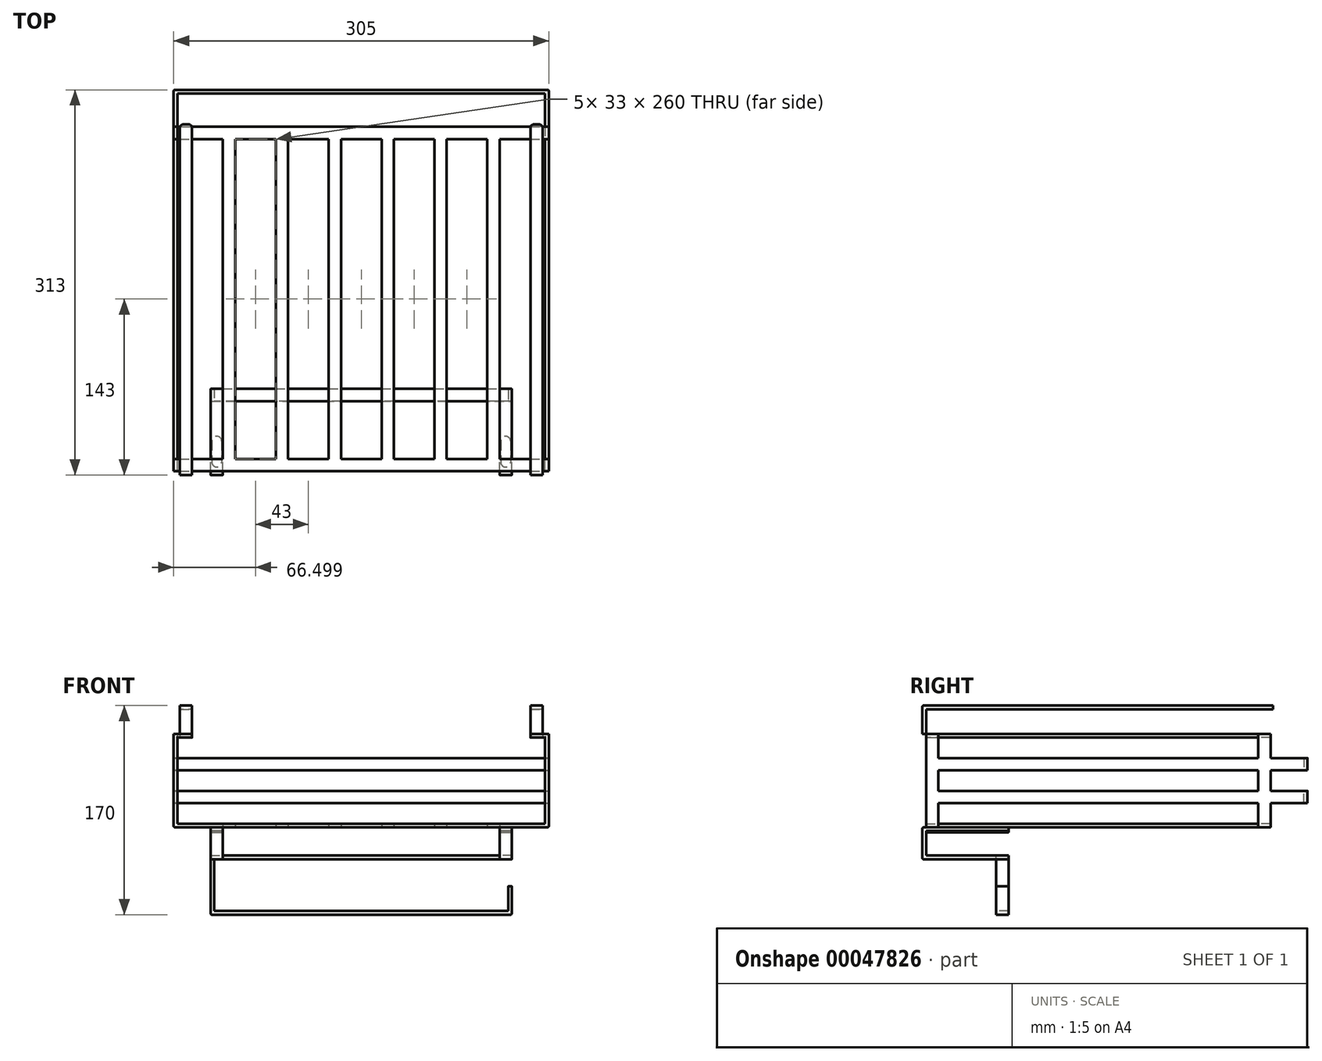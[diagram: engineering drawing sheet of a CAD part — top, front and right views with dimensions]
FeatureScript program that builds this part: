
annotation { "Feature Type Name" : "Feature", "Feature Type Description" : "" }
export const myFeature = defineFeature(function(context is Context, id is Id, definition is map)
    precondition{}
    {
        {
            var Q0;
            Q0=qCreatedBy(makeId("Top.planeOp"),FACE);
            var sketch = newSketch(context, id + "F0", { "sketchPlane" : qUnion([Q0])});
            skLineSegment(sketch, "E0.bottom", {"start": v(-169.28, 215.65) * mm, "end": v(135.72, 215.65) * mm});
            skLineSegment(sketch, "E0.top", {"start": v(-169.28, -94.35) * mm, "end": v(135.72, -94.35) * mm});
            skLineSegment(sketch, "E0.left", {"start": v(-169.28, 215.65) * mm, "end": v(-169.28, -94.35) * mm});
            skLineSegment(sketch, "E0.right", {"start": v(135.72, 215.65) * mm, "end": v(135.72, -94.35) * mm});
            skLineSegment(sketch, "E1", {"start": v(-169.28, -84.35) * mm, "end": v(135.72, -84.35) * mm});
            skLineSegment(sketch, "E2", {"start": v(-129.28, -84.35) * mm, "end": v(-129.28, 175.65) * mm});
            skLineSegment(sketch, "E3.0", {"start": v(-119.28, -84.35) * mm, "end": v(-119.28, 175.65) * mm});
            skLineSegment(sketch, "E4", {"start": v(-86.28, -84.35) * mm, "end": v(-86.28, 175.65) * mm});
            skLineSegment(sketch, "E5.0", {"start": v(-76.28, -84.35) * mm, "end": v(-76.28, 175.65) * mm});
            skLineSegment(sketch, "E6.0", {"start": v(-43.28, -84.35) * mm, "end": v(-43.28, 175.65) * mm});
            skLineSegment(sketch, "E7.0", {"start": v(-33.28, -84.35) * mm, "end": v(-33.28, 175.65) * mm});
            skLineSegment(sketch, "E8.0", {"start": v(-0.28, -84.35) * mm, "end": v(-0.28, 175.65) * mm});
            skLineSegment(sketch, "E9.0", {"start": v(9.72, -84.35) * mm, "end": v(9.72, 175.65) * mm});
            skLineSegment(sketch, "E10.0", {"start": v(42.72, -84.35) * mm, "end": v(42.72, 175.65) * mm});
            skLineSegment(sketch, "E11.0", {"start": v(52.72, -84.35) * mm, "end": v(52.72, 175.65) * mm});
            skLineSegment(sketch, "E12.0", {"start": v(85.72, -84.35) * mm, "end": v(85.72, 175.65) * mm});
            skLineSegment(sketch, "E13.0", {"start": v(95.72, -84.35) * mm, "end": v(95.72, 175.65) * mm});
            skLineSegment(sketch, "E14", {"start": v(-129.28, -42.82) * mm, "end": v(-169.28, -42.82) * mm, "construction": true});
            skLineSegment(sketch, "E15", {"start": v(95.72, -42.82) * mm, "end": v(135.72, -42.82) * mm, "construction": true});
            skLineSegment(sketch, "E16", {"start": v(-169.28, 175.65) * mm, "end": v(135.72, 175.65) * mm});
            skLineSegment(sketch, "E17.0", {"start": v(-169.28, 185.65) * mm, "end": v(135.72, 185.65) * mm});
            skPoint(sketch, "E18", {"position": v(-16.78, -94.35) * mm});
            skSolve(sketch);
        }
        {
            var Q0;
            {var subQ13=sQuery(id+"F0.wireOp",EDGE,"E17.0");Q0=makeQuery(id+"F0.imprint","IMPRINT",FACE,{"disambiguationData":[TD([[makeQuery(id+"F0.imprint","IMPRINT",EDGE,{"derivedFrom":subQ13}),-1.0]])]});}
            var Q1;
            {var subQ2=sQuery(id+"F0.wireOp",EDGE,"E2");Q1=makeQuery(id+"F0.imprint","IMPRINT",FACE,{"disambiguationData":[TD([[makeQuery(id+"F0.imprint","IMPRINT",EDGE,{"derivedFrom":subQ2}),-1.0]])]});}
            var Q2;
            {var subQ2=sQuery(id+"F0.wireOp",EDGE,"E4");Q2=makeQuery(id+"F0.imprint","IMPRINT",FACE,{"disambiguationData":[TD([[makeQuery(id+"F0.imprint","IMPRINT",EDGE,{"derivedFrom":subQ2}),-1.0]])]});}
            var Q3;
            {var subQ2=sQuery(id+"F0.wireOp",EDGE,"E6.0");Q3=makeQuery(id+"F0.imprint","IMPRINT",FACE,{"disambiguationData":[TD([[makeQuery(id+"F0.imprint","IMPRINT",EDGE,{"derivedFrom":subQ2}),-1.0]])]});}
            var Q4;
            {var subQ2=sQuery(id+"F0.wireOp",EDGE,"E8.0");Q4=makeQuery(id+"F0.imprint","IMPRINT",FACE,{"disambiguationData":[TD([[makeQuery(id+"F0.imprint","IMPRINT",EDGE,{"derivedFrom":subQ2}),-1.0]])]});}
            var Q5;
            {var subQ2=sQuery(id+"F0.wireOp",EDGE,"E10.0");Q5=makeQuery(id+"F0.imprint","IMPRINT",FACE,{"disambiguationData":[TD([[makeQuery(id+"F0.imprint","IMPRINT",EDGE,{"derivedFrom":subQ2}),-1.0]])]});}
            var Q6;
            {var subQ2=sQuery(id+"F0.wireOp",EDGE,"E12.0");Q6=makeQuery(id+"F0.imprint","IMPRINT",FACE,{"disambiguationData":[TD([[makeQuery(id+"F0.imprint","IMPRINT",EDGE,{"derivedFrom":subQ2}),-1.0]])]});}
            var Q7;
            {var subQ6=sQuery(id+"F0.wireOp",EDGE,"E0.top");Q7=makeQuery(id+"F0.imprint","IMPRINT",FACE,{"disambiguationData":[TD([[makeQuery(id+"F0.imprint","IMPRINT",EDGE,{"derivedFrom":subQ6}),1.0]])]});}
            extrude(context, id + "F1", {"entities" : qUnion([Q0, Q1, Q2, Q3, Q4, Q5, Q6, Q7]), "depth" : 3 * mm});
        }
        {
            var Q0;
            Q0=makeQuery(id+"F1.opExtrude","CAP_FACE",FACE,{"disambiguationData":[OSD([sQuery(id+"F0.wireOp",EDGE,"E0.top"),sQuery(id+"F0.wireOp",EDGE,"E0.left"),sQuery(id+"F0.wireOp",EDGE,"E0.right"),sQuery(id+"F0.wireOp",EDGE,"E1"),sQuery(id+"F0.wireOp",EDGE,"E2"),sQuery(id+"F0.wireOp",EDGE,"E3.0"),sQuery(id+"F0.wireOp",EDGE,"E4"),sQuery(id+"F0.wireOp",EDGE,"E5.0"),sQuery(id+"F0.wireOp",EDGE,"E6.0"),sQuery(id+"F0.wireOp",EDGE,"E7.0"),sQuery(id+"F0.wireOp",EDGE,"E8.0"),sQuery(id+"F0.wireOp",EDGE,"E9.0"),sQuery(id+"F0.wireOp",EDGE,"E10.0"),sQuery(id+"F0.wireOp",EDGE,"E11.0"),sQuery(id+"F0.wireOp",EDGE,"E12.0"),sQuery(id+"F0.wireOp",EDGE,"E13.0"),sQuery(id+"F0.wireOp",EDGE,"E16"),sQuery(id+"F0.wireOp",EDGE,"E17.0")])],"isStart":false});
            var sketch = newSketch(context, id + "F2", { "sketchPlane" : qUnion([Q0])});
            skLineSegment(sketch, "E19.bottom", {"start": v(-169.28, 185.65) * mm, "end": v(-166.28, 185.65) * mm});
            skLineSegment(sketch, "E19.top", {"start": v(-169.28, 175.65) * mm, "end": v(-166.28, 175.65) * mm});
            skLineSegment(sketch, "E19.left", {"start": v(-169.28, 185.65) * mm, "end": v(-169.28, 175.65) * mm});
            skLineSegment(sketch, "E19.right", {"start": v(-166.28, 185.65) * mm, "end": v(-166.28, 175.65) * mm});
            skLineSegment(sketch, "E20.bottom", {"start": v(-169.28, -94.35) * mm, "end": v(-166.28, -94.35) * mm});
            skLineSegment(sketch, "E20.top", {"start": v(-169.28, -84.35) * mm, "end": v(-166.28, -84.35) * mm});
            skLineSegment(sketch, "E20.left", {"start": v(-169.28, -94.35) * mm, "end": v(-169.28, -84.35) * mm});
            skLineSegment(sketch, "E20.right", {"start": v(-166.28, -94.35) * mm, "end": v(-166.28, -84.35) * mm});
            skLineSegment(sketch, "E21", {"start": v(-16.78, 152.07) * mm, "end": v(-16.78, 185.65) * mm, "construction": true});
            skLineSegment(sketch, "E22.MirrorCS", {"start": v(132.72, 185.65) * mm, "end": v(132.72, 175.65) * mm});
            skLineSegment(sketch, "E23.MirrorCS", {"start": v(135.72, 185.65) * mm, "end": v(135.72, 175.65) * mm});
            skLineSegment(sketch, "E24.MirrorCS", {"start": v(135.72, 185.65) * mm, "end": v(132.72, 185.65) * mm});
            skLineSegment(sketch, "E25.MirrorCS", {"start": v(135.72, 175.65) * mm, "end": v(132.72, 175.65) * mm});
            skLineSegment(sketch, "E26.MirrorCS", {"start": v(132.72, -94.35) * mm, "end": v(132.72, -84.35) * mm});
            skLineSegment(sketch, "E27.MirrorCS", {"start": v(135.72, -94.35) * mm, "end": v(135.72, -84.35) * mm});
            skLineSegment(sketch, "E28.MirrorCS", {"start": v(135.72, -84.35) * mm, "end": v(132.72, -84.35) * mm});
            skLineSegment(sketch, "E29.MirrorCS", {"start": v(135.72, -94.35) * mm, "end": v(132.72, -94.35) * mm});
            skSolve(sketch);
        }
        {
            var Q0;
            Q0=makeQuery(id+"F2.imprint","IMPRINT",FACE,{"disambiguationData":[TD([[makeQuery(id+"F2.imprint","IMPRINT",EDGE,{"derivedFrom":sQuery(id+"F2.wireOp",EDGE,"E19.bottom")}),-1.0]])]});
            var Q1;
            Q1=makeQuery(id+"F2.imprint","IMPRINT",FACE,{"disambiguationData":[TD([[makeQuery(id+"F2.imprint","IMPRINT",EDGE,{"derivedFrom":sQuery(id+"F2.wireOp",EDGE,"E22.MirrorCS")}),1.0]])]});
            var Q2;
            Q2=makeQuery(id+"F2.imprint","IMPRINT",FACE,{"disambiguationData":[TD([[makeQuery(id+"F2.imprint","IMPRINT",EDGE,{"derivedFrom":sQuery(id+"F2.wireOp",EDGE,"E26.MirrorCS")}),-1.0]])]});
            var Q3;
            Q3=makeQuery(id+"F2.imprint","IMPRINT",FACE,{"disambiguationData":[TD([[makeQuery(id+"F2.imprint","IMPRINT",EDGE,{"derivedFrom":sQuery(id+"F2.wireOp",EDGE,"E20.bottom")}),1.0]])]});
            extrude(context, id + "F3", {"entities" : qUnion([Q0, Q1, Q2, Q3]), "operationType" : NewBodyOperationType.ADD, "depth" : 70 * mm});
        }
        {
            var Q0;
            Q0=makeQuery(id+"F3.opExtrude","CAP_FACE",FACE,{"disambiguationData":[OSD([sQuery(id+"F2.wireOp",EDGE,"E19.bottom"),sQuery(id+"F2.wireOp",EDGE,"E19.top"),sQuery(id+"F2.wireOp",EDGE,"E19.left"),sQuery(id+"F2.wireOp",EDGE,"E19.right")])],"isStart":false});
            var sketch = newSketch(context, id + "F4", { "sketchPlane" : qUnion([Q0])});
            skLineSegment(sketch, "E30.bottom", {"start": v(-164.28, 185.65) * mm, "end": v(-154.28, 185.65) * mm});
            skLineSegment(sketch, "E30.top", {"start": v(-164.28, -94.35) * mm, "end": v(-154.28, -94.35) * mm});
            skLineSegment(sketch, "E30.left", {"start": v(-164.28, 185.65) * mm, "end": v(-164.28, -94.35) * mm});
            skLineSegment(sketch, "E30.right", {"start": v(-154.28, 185.65) * mm, "end": v(-154.28, -94.35) * mm});
            skLineSegment(sketch, "E31.MirrorCS", {"start": v(120.72, 185.65) * mm, "end": v(120.72, -94.35) * mm});
            skLineSegment(sketch, "E32.MirrorCS", {"start": v(130.72, 185.65) * mm, "end": v(130.72, -94.35) * mm});
            skLineSegment(sketch, "E33.MirrorCS", {"start": v(130.72, 185.65) * mm, "end": v(120.72, 185.65) * mm});
            skLineSegment(sketch, "E34.MirrorCS", {"start": v(130.72, -94.35) * mm, "end": v(120.72, -94.35) * mm});
            skLineSegment(sketch, "E35.bottom", {"start": v(-164.28, -94.35) * mm, "end": v(-169.28, -94.35) * mm});
            skLineSegment(sketch, "E35.top", {"start": v(-164.28, -84.35) * mm, "end": v(-169.28, -84.35) * mm});
            skLineSegment(sketch, "E35.left", {"start": v(-164.28, -94.35) * mm, "end": v(-164.28, -84.35) * mm});
            skLineSegment(sketch, "E35.right", {"start": v(-169.28, -94.35) * mm, "end": v(-169.28, -84.35) * mm});
            skLineSegment(sketch, "E36.MirrorCS", {"start": v(130.72, -84.35) * mm, "end": v(135.72, -84.35) * mm});
            skLineSegment(sketch, "E37.MirrorCS", {"start": v(135.72, -94.35) * mm, "end": v(135.72, -84.35) * mm});
            skLineSegment(sketch, "E38.MirrorCS", {"start": v(130.72, -94.35) * mm, "end": v(135.72, -94.35) * mm});
            skLineSegment(sketch, "E39.bottom", {"start": v(-164.28, 185.65) * mm, "end": v(-169.28, 185.65) * mm});
            skLineSegment(sketch, "E39.top", {"start": v(-164.28, 175.65) * mm, "end": v(-169.28, 175.65) * mm});
            skLineSegment(sketch, "E39.left", {"start": v(-164.28, 185.65) * mm, "end": v(-164.28, 175.65) * mm});
            skLineSegment(sketch, "E39.right", {"start": v(-169.28, 185.65) * mm, "end": v(-169.28, 175.65) * mm});
            skLineSegment(sketch, "E40.MirrorCS", {"start": v(130.72, 175.65) * mm, "end": v(135.72, 175.65) * mm});
            skLineSegment(sketch, "E41.MirrorCS", {"start": v(130.72, 185.65) * mm, "end": v(135.72, 185.65) * mm});
            skLineSegment(sketch, "E42.MirrorCS", {"start": v(135.72, 185.65) * mm, "end": v(135.72, 175.65) * mm});
            skLineSegment(sketch, "E43.bottom", {"start": v(-154.28, -94.35) * mm, "end": v(-164.28, -94.35) * mm});
            skLineSegment(sketch, "E43.top", {"start": v(-154.28, -97.35) * mm, "end": v(-164.28, -97.35) * mm});
            skLineSegment(sketch, "E43.left", {"start": v(-154.28, -94.35) * mm, "end": v(-154.28, -97.35) * mm});
            skLineSegment(sketch, "E43.right", {"start": v(-164.28, -94.35) * mm, "end": v(-164.28, -97.35) * mm});
            skLineSegment(sketch, "E44.top", {"start": v(130.72, -97.35) * mm, "end": v(120.72, -97.35) * mm});
            skLineSegment(sketch, "E44.left", {"start": v(130.72, -94.35) * mm, "end": v(130.72, -97.35) * mm});
            skLineSegment(sketch, "E44.right", {"start": v(120.72, -94.35) * mm, "end": v(120.72, -97.35) * mm});
            skSolve(sketch);
        }
        {
            var Q0;
            Q0=makeQuery(id+"F4.imprint","IMPRINT",FACE,{"disambiguationData":[TD([[makeQuery(id+"F4.imprint","IMPRINT",EDGE,{"derivedFrom":sQuery(id+"F4.wireOp",EDGE,"E30.bottom")}),-1.0]])]});
            var Q1;
            {var subQ1=sQuery(id+"F4.wireOp",EDGE,"E39.left");Q1=makeQuery(id+"F4.imprint","IMPRINT",FACE,{"disambiguationData":[TD([[makeQuery(id+"F4.imprint","IMPRINT",EDGE,{"derivedFrom":subQ1}),-1.0]])]});}
            var Q2;
            {var subQ1=sQuery(id+"F4.wireOp",EDGE,"E39.right");Q2=makeQuery(id+"F4.imprint","IMPRINT",FACE,{"disambiguationData":[TD([[makeQuery(id+"F4.imprint","IMPRINT",EDGE,{"derivedFrom":subQ1}),1.0]])]});}
            var Q3;
            Q3=makeQuery(id+"F4.imprint","IMPRINT",FACE,{"disambiguationData":[TD([[makeQuery(id+"F4.imprint","IMPRINT",EDGE,{"derivedFrom":sQuery(id+"F4.wireOp",EDGE,"E43.bottom")}),1.0]])]});
            var Q4;
            Q4=makeQuery(id+"F4.imprint","IMPRINT",FACE,{"disambiguationData":[TD([[makeQuery(id+"F4.imprint","IMPRINT",EDGE,{"derivedFrom":sQuery(id+"F4.wireOp",EDGE,"E34.MirrorCS")}),1.0]])]});
            var Q5;
            Q5=makeQuery(id+"F4.imprint","IMPRINT",FACE,{"disambiguationData":[TD([[makeQuery(id+"F4.imprint","IMPRINT",EDGE,{"derivedFrom":sQuery(id+"F4.wireOp",EDGE,"E31.MirrorCS")}),1.0]])]});
            var Q6;
            {var subQ1=sQuery(id+"F4.wireOp",EDGE,"E36.MirrorCS");Q6=makeQuery(id+"F4.imprint","IMPRINT",FACE,{"disambiguationData":[TD([[makeQuery(id+"F4.imprint","IMPRINT",EDGE,{"derivedFrom":subQ1}),-1.0]])]});}
            var Q7;
            {var subQ1=sQuery(id+"F4.wireOp",EDGE,"E40.MirrorCS");Q7=makeQuery(id+"F4.imprint","IMPRINT",FACE,{"disambiguationData":[TD([[makeQuery(id+"F4.imprint","IMPRINT",EDGE,{"derivedFrom":subQ1}),1.0]])]});}
            var Q8;
            Q8=makeQuery(id+"F4.imprint","IMPRINT",FACE,{"disambiguationData":[TD([[makeQuery(id+"F4.imprint","IMPRINT",EDGE,{"derivedFrom":sQuery(id+"F4.wireOp",EDGE,"E35.bottom")}),-1.0]])]});
            extrude(context, id + "F5", {"entities" : qUnion([Q0, Q1, Q2, Q3, Q4, Q5, Q6, Q7, Q8]), "operationType" : NewBodyOperationType.ADD, "depth" : 3 * mm});
        }
        {
            var Q0;
            Q0=makeQuery(id+"F5.opExtrude","CAP_FACE",FACE,{"disambiguationData":[OSD([sQuery(id+"F4.wireOp",EDGE,"E30.bottom"),sQuery(id+"F4.wireOp",EDGE,"E30.top"),sQuery(id+"F4.wireOp",EDGE,"E30.left"),sQuery(id+"F4.wireOp",EDGE,"E30.right")])],"isStart":false});
            var sketch = newSketch(context, id + "F6", { "sketchPlane" : qUnion([Q0])});
            skLineSegment(sketch, "E45.bottom", {"start": v(-154.28, -97.35) * mm, "end": v(-164.28, -97.35) * mm});
            skLineSegment(sketch, "E45.top", {"start": v(-154.28, -94.35) * mm, "end": v(-164.28, -94.35) * mm});
            skLineSegment(sketch, "E45.left", {"start": v(-154.28, -97.35) * mm, "end": v(-154.28, -94.35) * mm});
            skLineSegment(sketch, "E45.right", {"start": v(-164.28, -97.35) * mm, "end": v(-164.28, -94.35) * mm});
            skLineSegment(sketch, "E46.MirrorCS", {"start": v(120.72, -94.35) * mm, "end": v(130.72, -94.35) * mm});
            skLineSegment(sketch, "E47.MirrorCS", {"start": v(130.72, -97.35) * mm, "end": v(130.72, -94.35) * mm});
            skLineSegment(sketch, "E48.MirrorCS", {"start": v(120.72, -97.35) * mm, "end": v(120.72, -94.35) * mm});
            skLineSegment(sketch, "E49.MirrorCS", {"start": v(120.72, -97.35) * mm, "end": v(130.72, -97.35) * mm});
            skSolve(sketch);
        }
        {
            var Q0;
            Q0=makeQuery(id+"F6.imprint","IMPRINT",FACE,{"disambiguationData":[TD([[makeQuery(id+"F6.imprint","IMPRINT",EDGE,{"derivedFrom":sQuery(id+"F6.wireOp",EDGE,"E45.bottom")}),-1.0]])]});
            var Q1;
            Q1=makeQuery(id+"F6.imprint","IMPRINT",FACE,{"disambiguationData":[TD([[makeQuery(id+"F6.imprint","IMPRINT",EDGE,{"derivedFrom":sQuery(id+"F6.wireOp",EDGE,"E46.MirrorCS")}),-1.0]])]});
            extrude(context, id + "F7", {"entities" : qUnion([Q0, Q1]), "operationType" : NewBodyOperationType.ADD, "depth" : 20 * mm});
        }
        {
            var Q0;
            Q0=makeQuery(id+"F7.opExtrude","CAP_FACE",FACE,{"disambiguationData":[OSD([sQuery(id+"F6.wireOp",EDGE,"E45.bottom"),sQuery(id+"F6.wireOp",EDGE,"E45.top"),sQuery(id+"F6.wireOp",EDGE,"E45.left"),sQuery(id+"F6.wireOp",EDGE,"E45.right")])],"isStart":false});
            var sketch = newSketch(context, id + "F8", { "sketchPlane" : qUnion([Q0])});
            skLineSegment(sketch, "E50.bottom", {"start": v(-164.28, -97.35) * mm, "end": v(-154.28, -97.35) * mm});
            skLineSegment(sketch, "E50.top", {"start": v(-164.28, 187.65) * mm, "end": v(-154.28, 187.65) * mm});
            skLineSegment(sketch, "E50.left", {"start": v(-164.28, -97.35) * mm, "end": v(-164.28, 187.65) * mm});
            skLineSegment(sketch, "E50.right", {"start": v(-154.28, -97.35) * mm, "end": v(-154.28, 187.65) * mm});
            skLineSegment(sketch, "E51.MirrorCS", {"start": v(120.72, -97.35) * mm, "end": v(120.72, 187.65) * mm});
            skLineSegment(sketch, "E52.MirrorCS", {"start": v(130.72, 187.65) * mm, "end": v(120.72, 187.65) * mm});
            skLineSegment(sketch, "E53.MirrorCS", {"start": v(130.72, -97.35) * mm, "end": v(130.72, 187.65) * mm});
            skLineSegment(sketch, "E54.MirrorCS", {"start": v(130.72, -97.35) * mm, "end": v(120.72, -97.35) * mm});
            skPoint(sketch, "E55", {"position": v(-154.28, 45.15) * mm});
            skSolve(sketch);
        }
        {
            var Q0;
            {var subQ1=sQuery(id+"F8.wireOp",EDGE,"E50.top");Q0=makeQuery(id+"F8.imprint","IMPRINT",FACE,{"disambiguationData":[TD([[makeQuery(id+"F8.imprint","IMPRINT",EDGE,{"derivedFrom":subQ1}),-1.0]])]});}
            var Q1;
            Q1=makeQuery(id+"F8.imprint","IMPRINT",FACE,{"disambiguationData":[TD([[makeQuery(id+"F8.imprint","IMPRINT",EDGE,{"derivedFrom":sQuery(id+"F8.wireOp",EDGE,"E51.MirrorCS")}),-1.0]])]});
            var Q2;
            {var subQ2=sQuery(id+"F8.wireOp",EDGE,"E50.bottom");Q2=makeQuery(id+"F8.imprint","IMPRINT",FACE,{"disambiguationData":[TD([[makeQuery(id+"F8.imprint","IMPRINT",EDGE,{"derivedFrom":subQ2}),1.0]])]});}
            var Q3;
            {var subQ2=sQuery(id+"F8.wireOp",EDGE,"E50.bottom");Q3=makeQuery(id+"F8.imprint","IMPRINT",FACE,{"disambiguationData":[TD([[makeQuery(id+"F8.imprint","IMPRINT",EDGE,{"derivedFrom":subQ2}),-1.0]])]});}
            extrude(context, id + "F9", {"entities" : qUnion([Q0, Q1, Q2, Q3]), "operationType" : NewBodyOperationType.ADD, "depth" : 3 * mm});
        }
        {
            var Q0;
            Q0=makeQuery(id+"F5.boolean.opBoolean","MERGE",FACE,{"derivedFrom":[makeQuery(id+"F3.boolean.opBoolean","MERGE",FACE,{"derivedFrom":[makeQuery(id+"F1.opExtrude","SWEPT_FACE",FACE,{"disambiguationData":[OSD([sQuery(id+"F0.wireOp",EDGE,"E17.0")])]}),makeQuery(id+"F3.opExtrude","SWEPT_FACE",FACE,{"disambiguationData":[OSD([sQuery(id+"F2.wireOp",EDGE,"E19.bottom")])]}),makeQuery(id+"F3.opExtrude","SWEPT_FACE",FACE,{"disambiguationData":[OSD([sQuery(id+"F2.wireOp",EDGE,"E24.MirrorCS")])]})]}),makeQuery(id+"F5.opExtrude","SWEPT_FACE",FACE,{"disambiguationData":[OSD([sQuery(id+"F4.wireOp",EDGE,"E30.bottom")])]}),makeQuery(id+"F5.opExtrude","SWEPT_FACE",FACE,{"disambiguationData":[OSD([sQuery(id+"F4.wireOp",EDGE,"E33.MirrorCS")])]})]});
            var sketch = newSketch(context, id + "F10", { "sketchPlane" : qUnion([Q0])});
            skLineSegment(sketch, "E56", {"start": v(166.28, 3) * mm, "end": v(169.28, 3) * mm, "construction": true});
            skLineSegment(sketch, "E57", {"start": v(166.28, 73) * mm, "end": v(169.28, 73) * mm, "construction": true});
            skLineSegment(sketch, "E58.bottom", {"start": v(169.28, 56.33) * mm, "end": v(166.28, 56.33) * mm});
            skLineSegment(sketch, "E58.top", {"start": v(169.28, 46.33) * mm, "end": v(166.28, 46.33) * mm});
            skLineSegment(sketch, "E58.left", {"start": v(169.28, 56.33) * mm, "end": v(169.28, 46.33) * mm});
            skLineSegment(sketch, "E58.right", {"start": v(166.28, 56.33) * mm, "end": v(166.28, 46.33) * mm});
            skLineSegment(sketch, "E59.bottom", {"start": v(169.28, 29.67) * mm, "end": v(166.28, 29.67) * mm});
            skLineSegment(sketch, "E59.top", {"start": v(169.28, 19.67) * mm, "end": v(166.28, 19.67) * mm});
            skLineSegment(sketch, "E59.left", {"start": v(169.28, 29.67) * mm, "end": v(169.28, 19.67) * mm});
            skLineSegment(sketch, "E59.right", {"start": v(166.28, 29.67) * mm, "end": v(166.28, 19.67) * mm});
            skLineSegment(sketch, "E60", {"start": v(167.78, 73) * mm, "end": v(167.78, 56.33) * mm, "construction": true});
            skLineSegment(sketch, "E61", {"start": v(167.78, 46.33) * mm, "end": v(167.78, 29.67) * mm, "construction": true});
            skLineSegment(sketch, "E62", {"start": v(167.78, 19.67) * mm, "end": v(167.78, 3) * mm, "construction": true});
            skLineSegment(sketch, "E63", {"start": v(16.78, 3) * mm, "end": v(16.78, 25.42) * mm, "construction": true});
            skLineSegment(sketch, "E64.MirrorCS", {"start": v(-135.72, 19.67) * mm, "end": v(-132.72, 19.67) * mm});
            skLineSegment(sketch, "E65.MirrorCS", {"start": v(-135.72, 29.67) * mm, "end": v(-132.72, 29.67) * mm});
            skLineSegment(sketch, "E66.MirrorCS", {"start": v(-132.72, 29.67) * mm, "end": v(-132.72, 19.67) * mm});
            skLineSegment(sketch, "E67.MirrorCS", {"start": v(-135.72, 29.67) * mm, "end": v(-135.72, 19.67) * mm});
            skLineSegment(sketch, "E68.MirrorCS", {"start": v(-135.72, 46.33) * mm, "end": v(-132.72, 46.33) * mm});
            skLineSegment(sketch, "E69.MirrorCS", {"start": v(-132.72, 56.33) * mm, "end": v(-132.72, 46.33) * mm});
            skLineSegment(sketch, "E70.MirrorCS", {"start": v(-135.72, 56.33) * mm, "end": v(-135.72, 46.33) * mm});
            skLineSegment(sketch, "E71.MirrorCS", {"start": v(-135.72, 56.33) * mm, "end": v(-132.72, 56.33) * mm});
            skSolve(sketch);
        }
        {
            var Q0;
            Q0=makeQuery(id+"F10.imprint","IMPRINT",FACE,{"disambiguationData":[TD([[makeQuery(id+"F10.imprint","IMPRINT",EDGE,{"derivedFrom":sQuery(id+"F10.wireOp",EDGE,"E58.bottom")}),1.0]])]});
            var Q1;
            Q1=makeQuery(id+"F10.imprint","IMPRINT",FACE,{"disambiguationData":[TD([[makeQuery(id+"F10.imprint","IMPRINT",EDGE,{"derivedFrom":sQuery(id+"F10.wireOp",EDGE,"E59.bottom")}),1.0]])]});
            var Q2;
            Q2=makeQuery(id+"F10.imprint","IMPRINT",FACE,{"disambiguationData":[TD([[makeQuery(id+"F10.imprint","IMPRINT",EDGE,{"derivedFrom":sQuery(id+"F10.wireOp",EDGE,"E68.MirrorCS")}),1.0]])]});
            var Q3;
            Q3=makeQuery(id+"F10.imprint","IMPRINT",FACE,{"disambiguationData":[TD([[makeQuery(id+"F10.imprint","IMPRINT",EDGE,{"derivedFrom":sQuery(id+"F10.wireOp",EDGE,"E64.MirrorCS")}),1.0]])]});
            var Q4;
            {var subQ0=sQuery(id+"F0.wireOp",EDGE,"E1");Q4=makeQuery(id+"F3.boolean.opBoolean","MERGE",FACE,{"derivedFrom":[makeQuery(id+"F1.opExtrude","SWEPT_FACE",FACE,{"disambiguationData":[OSD([subQ0]),TDD([makeQuery(id+"F0.imprint","IMPRINT",EDGE,{"disambiguationData":[TD([[makeQuery(id+"F0.imprint","INTERSECT",VERTEX,{"derivedFrom":[sQuery(id+"F0.wireOp",EDGE,"E0.left"),subQ0]}),-1.0]])],"derivedFrom":subQ0})])]}),makeQuery(id+"F3.opExtrude","SWEPT_FACE",FACE,{"disambiguationData":[OSD([sQuery(id+"F2.wireOp",EDGE,"E20.top")])]})]});}
            extrude(context, id + "F11", {"entities" : qUnion([Q0, Q1, Q2, Q3]), "operationType" : NewBodyOperationType.ADD, "depth" : 30 * mm, "hasSecondDirection" : true, "secondDirectionBound" : SecondDirectionBoundingType.UP_TO_SURFACE, "secondDirectionOppositeDirection" : true, "secondDirectionBoundEntityFace" : qUnion([Q4]), "secondDirectionDepth" : 25 * mm});
        }
        {
            var Q0;
            Q0=makeQuery(id+"F11.boolean.opBoolean","MERGE",FACE,{"derivedFrom":[makeQuery(id+"F3.opExtrude","SWEPT_FACE",FACE,{"disambiguationData":[OSD([sQuery(id+"F2.wireOp",EDGE,"E19.right")])]}),makeQuery(id+"F3.opExtrude","SWEPT_FACE",FACE,{"disambiguationData":[OSD([sQuery(id+"F2.wireOp",EDGE,"E20.right")])]}),makeQuery(id+"F11.opExtrude","SWEPT_FACE",FACE,{"disambiguationData":[OSD([sQuery(id+"F10.wireOp",EDGE,"E58.right")])]}),makeQuery(id+"F11.opExtrude","SWEPT_FACE",FACE,{"disambiguationData":[OSD([sQuery(id+"F10.wireOp",EDGE,"E59.right")])]})]});
            var sketch = newSketch(context, id + "F12", { "sketchPlane" : qUnion([Q0])});
            skLineSegment(sketch, "E72.bottom", {"start": v(215.65, 56.33) * mm, "end": v(212.65, 56.33) * mm});
            skLineSegment(sketch, "E72.top", {"start": v(215.65, 46.33) * mm, "end": v(212.65, 46.33) * mm});
            skLineSegment(sketch, "E72.left", {"start": v(215.65, 56.33) * mm, "end": v(215.65, 46.33) * mm});
            skLineSegment(sketch, "E72.right", {"start": v(212.65, 56.33) * mm, "end": v(212.65, 46.33) * mm});
            skLineSegment(sketch, "E73.bottom", {"start": v(215.65, 19.67) * mm, "end": v(212.65, 19.67) * mm});
            skLineSegment(sketch, "E73.top", {"start": v(215.65, 29.67) * mm, "end": v(212.65, 29.67) * mm});
            skLineSegment(sketch, "E73.left", {"start": v(215.65, 19.67) * mm, "end": v(215.65, 29.67) * mm});
            skLineSegment(sketch, "E73.right", {"start": v(212.65, 19.67) * mm, "end": v(212.65, 29.67) * mm});
            skSolve(sketch);
        }
        {
            var Q0;
            Q0=makeQuery(id+"F12.imprint","IMPRINT",FACE,{"disambiguationData":[TD([[makeQuery(id+"F12.imprint","IMPRINT",EDGE,{"derivedFrom":sQuery(id+"F12.wireOp",EDGE,"E72.bottom")}),1.0]])]});
            var Q1;
            Q1=makeQuery(id+"F12.imprint","IMPRINT",FACE,{"disambiguationData":[TD([[makeQuery(id+"F12.imprint","IMPRINT",EDGE,{"derivedFrom":sQuery(id+"F12.wireOp",EDGE,"E73.bottom")}),-1.0]])]});
            var Q2;
            Q2=makeQuery(id+"F11.boolean.opBoolean","MERGE",FACE,{"derivedFrom":[makeQuery(id+"F3.opExtrude","SWEPT_FACE",FACE,{"disambiguationData":[OSD([sQuery(id+"F2.wireOp",EDGE,"E22.MirrorCS")])]}),makeQuery(id+"F3.opExtrude","SWEPT_FACE",FACE,{"disambiguationData":[OSD([sQuery(id+"F2.wireOp",EDGE,"E26.MirrorCS")])]}),makeQuery(id+"F11.opExtrude","SWEPT_FACE",FACE,{"disambiguationData":[OSD([sQuery(id+"F10.wireOp",EDGE,"E66.MirrorCS")])]}),makeQuery(id+"F11.opExtrude","SWEPT_FACE",FACE,{"disambiguationData":[OSD([sQuery(id+"F10.wireOp",EDGE,"E69.MirrorCS")])]})]});
            extrude(context, id + "F13", {"entities" : qUnion([Q0, Q1]), "operationType" : NewBodyOperationType.ADD, "endBound" : BoundingType.UP_TO_SURFACE, "endBoundEntityFace" : qUnion([Q2]), "depth" : 25 * mm});
        }
        {
            var Q0;
            {var subQ0=sQuery(id+"F0.wireOp",EDGE,"E0.left");Q0=makeQuery(id+"F1.opExtrude","CAP_EDGE",EDGE,{"disambiguationData":[OSD([subQ0]),TDD([makeQuery(id+"F0.imprint","IMPRINT",EDGE,{"disambiguationData":[TD([[makeQuery(id+"F0.imprint","INTERSECT",VERTEX,{"derivedFrom":[subQ0,sQuery(id+"F0.wireOp",EDGE,"E16")]}),1.0]])],"derivedFrom":subQ0})])],"isStart":true});}
            var Q1;
            {var subQ0=sQuery(id+"F0.wireOp",EDGE,"E0.left");Q1=makeQuery(id+"F1.opExtrude","CAP_EDGE",EDGE,{"disambiguationData":[OSD([subQ0]),TDD([makeQuery(id+"F0.imprint","IMPRINT",EDGE,{"disambiguationData":[TD([[makeQuery(id+"F0.imprint","INTERSECT",VERTEX,{"derivedFrom":[sQuery(id+"F0.wireOp",EDGE,"E0.top"),subQ0]}),1.0]])],"derivedFrom":subQ0})])],"isStart":true});}
            var Q2;
            {var subQ0=sQuery(id+"F0.wireOp",EDGE,"E0.right");Q2=makeQuery(id+"F1.opExtrude","CAP_EDGE",EDGE,{"disambiguationData":[OSD([subQ0]),TDD([makeQuery(id+"F0.imprint","IMPRINT",EDGE,{"disambiguationData":[TD([[makeQuery(id+"F0.imprint","INTERSECT",VERTEX,{"derivedFrom":[sQuery(id+"F0.wireOp",EDGE,"E0.top"),subQ0]}),1.0]])],"derivedFrom":subQ0})])],"isStart":true});}
            var Q3;
            {var subQ0=sQuery(id+"F0.wireOp",EDGE,"E0.right");Q3=makeQuery(id+"F1.opExtrude","CAP_EDGE",EDGE,{"disambiguationData":[OSD([subQ0]),TDD([makeQuery(id+"F0.imprint","IMPRINT",EDGE,{"disambiguationData":[TD([[makeQuery(id+"F0.imprint","INTERSECT",VERTEX,{"derivedFrom":[subQ0,sQuery(id+"F0.wireOp",EDGE,"E16")]}),1.0]])],"derivedFrom":subQ0})])],"isStart":true});}
            var Q4;
            Q4=makeQuery(id+"F11.opExtrude","CAP_EDGE",EDGE,{"disambiguationData":[OSD([sQuery(id+"F10.wireOp",EDGE,"E67.MirrorCS")])],"isStart":false});
            var Q5;
            Q5=makeQuery(id+"F11.opExtrude","CAP_EDGE",EDGE,{"disambiguationData":[OSD([sQuery(id+"F10.wireOp",EDGE,"E70.MirrorCS")])],"isStart":false});
            var Q6;
            Q6=makeQuery(id+"F11.opExtrude","CAP_EDGE",EDGE,{"disambiguationData":[OSD([sQuery(id+"F10.wireOp",EDGE,"E58.left")])],"isStart":false});
            var Q7;
            Q7=makeQuery(id+"F11.opExtrude","CAP_EDGE",EDGE,{"disambiguationData":[OSD([sQuery(id+"F10.wireOp",EDGE,"E59.left")])],"isStart":false});
            var Q8;
            Q8=makeQuery(id+"F5.opExtrude","CAP_EDGE",EDGE,{"disambiguationData":[OSD([sQuery(id+"F4.wireOp",EDGE,"E30.left")])],"isStart":false});
            var Q9;
            Q9=makeQuery(id+"F9.opExtrude","CAP_EDGE",EDGE,{"disambiguationData":[OSD([sQuery(id+"F8.wireOp",EDGE,"E50.bottom")])],"isStart":false});
            var Q10;
            Q10=makeQuery(id+"F9.opExtrude","CAP_EDGE",EDGE,{"disambiguationData":[OSD([sQuery(id+"F8.wireOp",EDGE,"E54.MirrorCS")])],"isStart":false});
            var Q11;
            Q11=makeQuery(id+"F5.opExtrude","CAP_EDGE",EDGE,{"disambiguationData":[OSD([sQuery(id+"F4.wireOp",EDGE,"E32.MirrorCS")])],"isStart":false});
            var Q12;
            Q12=makeQuery(id+"F5.opExtrude","CAP_EDGE",EDGE,{"disambiguationData":[OSD([sQuery(id+"F4.wireOp",EDGE,"E30.top")])],"isStart":true});
            var Q13;
            Q13=makeQuery(id+"F5.opExtrude","CAP_EDGE",EDGE,{"disambiguationData":[OSD([sQuery(id+"F4.wireOp",EDGE,"E34.MirrorCS")])],"isStart":true});
            fillet(context, id + "F14", {"entities" : qUnion([Q0, Q1, Q2, Q3, Q4, Q5, Q6, Q7, Q8, Q9, Q10, Q11, Q12, Q13]), "radius" : 1 * mm, "tangentPropagation" : true, "allowEdgeOverflow" : false});
        }
        {
            var Q0;
            Q0=makeQuery(id+"F9.opExtrude","SWEPT_EDGE",EDGE,{"disambiguationData":[OSD([sQuery(id+"F8.wireOp",EDGE,"E50.top"),sQuery(id+"F8.wireOp",EDGE,"E50.right")])]});
            var Q1;
            Q1=makeQuery(id+"F9.opExtrude","SWEPT_EDGE",EDGE,{"disambiguationData":[OSD([sQuery(id+"F8.wireOp",EDGE,"E50.top"),sQuery(id+"F8.wireOp",EDGE,"E50.left")])]});
            var Q2;
            Q2=makeQuery(id+"F9.opExtrude","SWEPT_EDGE",EDGE,{"disambiguationData":[OSD([sQuery(id+"F8.wireOp",EDGE,"E51.MirrorCS"),sQuery(id+"F8.wireOp",EDGE,"E52.MirrorCS")])]});
            var Q3;
            Q3=makeQuery(id+"F9.opExtrude","SWEPT_EDGE",EDGE,{"disambiguationData":[OSD([sQuery(id+"F8.wireOp",EDGE,"E52.MirrorCS"),sQuery(id+"F8.wireOp",EDGE,"E53.MirrorCS")])]});
            fillet(context, id + "F15", {"entities" : qUnion([Q0, Q1, Q2, Q3]), "radius" : 3 * mm, "tangentPropagation" : true, "allowEdgeOverflow" : false});
        }
        {
            var Q0;
            Q0=qCreatedBy(makeId("Top.planeOp"),FACE);
            var sketch = newSketch(context, id + "F16", { "sketchPlane" : qUnion([Q0])});
            skLineSegment(sketch, "E74.bottom", {"start": v(-129.28, -97.35) * mm, "end": v(-139.28, -97.35) * mm});
            skLineSegment(sketch, "E74.top", {"start": v(-129.28, -27.35) * mm, "end": v(-139.28, -27.35) * mm});
            skLineSegment(sketch, "E74.left", {"start": v(-129.28, -97.35) * mm, "end": v(-129.28, -27.35) * mm});
            skLineSegment(sketch, "E74.right", {"start": v(-139.28, -97.35) * mm, "end": v(-139.28, -27.35) * mm});
            skLineSegment(sketch, "E75", {"start": v(-139.28, -115.8) * mm, "end": v(105.72, -115.8) * mm, "construction": true});
            skLineSegment(sketch, "E76", {"start": v(-16.78, -115.8) * mm, "end": v(-16.78, -137.19) * mm, "construction": true});
            skLineSegment(sketch, "E77.MirrorCS", {"start": v(95.72, -97.35) * mm, "end": v(95.72, -27.35) * mm});
            skLineSegment(sketch, "E78.MirrorCS", {"start": v(95.72, -27.35) * mm, "end": v(105.72, -27.35) * mm});
            skLineSegment(sketch, "E79.MirrorCS", {"start": v(105.72, -97.35) * mm, "end": v(105.72, -27.35) * mm});
            skLineSegment(sketch, "E80.MirrorCS", {"start": v(95.72, -97.35) * mm, "end": v(105.72, -97.35) * mm});
            skSolve(sketch);
        }
        {
            var Q0;
            Q0=makeQuery(id+"F16.imprint","IMPRINT",FACE,{"disambiguationData":[TD([[makeQuery(id+"F16.imprint","IMPRINT",EDGE,{"derivedFrom":sQuery(id+"F16.wireOp",EDGE,"E74.bottom")}),-1.0]])]});
            var Q1;
            Q1=makeQuery(id+"F16.imprint","IMPRINT",FACE,{"disambiguationData":[TD([[makeQuery(id+"F16.imprint","IMPRINT",EDGE,{"derivedFrom":sQuery(id+"F16.wireOp",EDGE,"E77.MirrorCS")}),-1.0]])]});
            extrude(context, id + "F17", {"entities" : qUnion([Q0, Q1]), "oppositeDirection" : true, "depth" : 3 * mm});
        }
        {
            var Q0;
            Q0=makeQuery(id+"F17.opExtrude","CAP_FACE",FACE,{"disambiguationData":[OSD([sQuery(id+"F16.wireOp",EDGE,"E74.bottom"),sQuery(id+"F16.wireOp",EDGE,"E74.top"),sQuery(id+"F16.wireOp",EDGE,"E74.left"),sQuery(id+"F16.wireOp",EDGE,"E74.right")])],"isStart":false});
            var sketch = newSketch(context, id + "F18", { "sketchPlane" : qUnion([Q0])});
            skLineSegment(sketch, "E81.bottom", {"start": v(-139.28, 97.35) * mm, "end": v(-129.28, 97.35) * mm});
            skLineSegment(sketch, "E81.top", {"start": v(-139.28, 94.35) * mm, "end": v(-129.28, 94.35) * mm});
            skLineSegment(sketch, "E81.left", {"start": v(-139.28, 97.35) * mm, "end": v(-139.28, 94.35) * mm});
            skLineSegment(sketch, "E81.right", {"start": v(-129.28, 97.35) * mm, "end": v(-129.28, 94.35) * mm});
            skLineSegment(sketch, "E82.MirrorCS", {"start": v(105.72, 97.35) * mm, "end": v(95.72, 97.35) * mm});
            skLineSegment(sketch, "E83.MirrorCS", {"start": v(105.72, 97.35) * mm, "end": v(105.72, 94.35) * mm});
            skLineSegment(sketch, "E84.MirrorCS", {"start": v(105.72, 94.35) * mm, "end": v(95.72, 94.35) * mm});
            skLineSegment(sketch, "E85.MirrorCS", {"start": v(95.72, 97.35) * mm, "end": v(95.72, 94.35) * mm});
            skSolve(sketch);
        }
        {
            var Q0;
            Q0=makeQuery(id+"F18.imprint","IMPRINT",FACE,{"disambiguationData":[TD([[makeQuery(id+"F18.imprint","IMPRINT",EDGE,{"derivedFrom":sQuery(id+"F18.wireOp",EDGE,"E81.bottom")}),1.0]])]});
            var Q1;
            Q1=makeQuery(id+"F18.imprint","IMPRINT",FACE,{"disambiguationData":[TD([[makeQuery(id+"F18.imprint","IMPRINT",EDGE,{"derivedFrom":sQuery(id+"F18.wireOp",EDGE,"E82.MirrorCS")}),1.0]])]});
            extrude(context, id + "F19", {"entities" : qUnion([Q0, Q1]), "operationType" : NewBodyOperationType.ADD, "depth" : 20 * mm});
        }
        {
            var Q0;
            Q0=makeQuery(id+"F19.opExtrude","CAP_FACE",FACE,{"disambiguationData":[OSD([sQuery(id+"F18.wireOp",EDGE,"E81.bottom"),sQuery(id+"F18.wireOp",EDGE,"E81.top"),sQuery(id+"F18.wireOp",EDGE,"E81.left"),sQuery(id+"F18.wireOp",EDGE,"E81.right")])],"isStart":false});
            var sketch = newSketch(context, id + "F20", { "sketchPlane" : qUnion([Q0])});
            skLineSegment(sketch, "E86.bottom", {"start": v(-139.28, 97.35) * mm, "end": v(-129.28, 97.35) * mm});
            skLineSegment(sketch, "E86.top", {"start": v(-139.28, 27.35) * mm, "end": v(-129.28, 27.35) * mm});
            skLineSegment(sketch, "E86.left", {"start": v(-139.28, 97.35) * mm, "end": v(-139.28, 27.35) * mm});
            skLineSegment(sketch, "E86.right", {"start": v(-129.28, 97.35) * mm, "end": v(-129.28, 27.35) * mm});
            skLineSegment(sketch, "E87.MirrorCS", {"start": v(105.72, 97.35) * mm, "end": v(95.72, 97.35) * mm});
            skLineSegment(sketch, "E88.MirrorCS", {"start": v(95.72, 97.35) * mm, "end": v(95.72, 27.35) * mm});
            skLineSegment(sketch, "E89.MirrorCS", {"start": v(105.72, 97.35) * mm, "end": v(105.72, 27.35) * mm});
            skLineSegment(sketch, "E90.MirrorCS", {"start": v(105.72, 27.35) * mm, "end": v(95.72, 27.35) * mm});
            skSolve(sketch);
        }
        {
            var Q0;
            Q0=makeQuery(id+"F20.imprint","IMPRINT",FACE,{"disambiguationData":[TD([[makeQuery(id+"F20.imprint","IMPRINT",EDGE,{"derivedFrom":sQuery(id+"F20.wireOp",EDGE,"E87.MirrorCS")}),1.0]])]});
            var Q1;
            {var subQ2=sQuery(id+"F20.wireOp",EDGE,"E86.top");Q1=makeQuery(id+"F20.imprint","IMPRINT",FACE,{"disambiguationData":[TD([[makeQuery(id+"F20.imprint","IMPRINT",EDGE,{"derivedFrom":subQ2}),1.0]])]});}
            var Q2;
            {var subQ2=sQuery(id+"F20.wireOp",EDGE,"E86.bottom");Q2=makeQuery(id+"F20.imprint","IMPRINT",FACE,{"disambiguationData":[TD([[makeQuery(id+"F20.imprint","IMPRINT",EDGE,{"derivedFrom":subQ2}),1.0]])]});}
            extrude(context, id + "F21", {"entities" : qUnion([Q0, Q1, Q2]), "operationType" : NewBodyOperationType.ADD, "depth" : 3 * mm});
        }
        {
            var Q0;
            Q0=makeQuery(id+"F21.boolean.opBoolean","MERGE",FACE,{"derivedFrom":[makeQuery(id+"F19.boolean.opBoolean","MERGE",FACE,{"derivedFrom":[makeQuery(id+"F17.opExtrude","SWEPT_FACE",FACE,{"disambiguationData":[OSD([sQuery(id+"F16.wireOp",EDGE,"E74.left")])]}),makeQuery(id+"F19.opExtrude","SWEPT_FACE",FACE,{"disambiguationData":[OSD([sQuery(id+"F18.wireOp",EDGE,"E81.right")])]})]}),makeQuery(id+"F21.opExtrude","SWEPT_FACE",FACE,{"disambiguationData":[OSD([sQuery(id+"F20.wireOp",EDGE,"E86.right")])]})]});
            var sketch = newSketch(context, id + "F22", { "sketchPlane" : qUnion([Q0])});
            skLineSegment(sketch, "E91.bottom", {"start": v(-27.35, -26) * mm, "end": v(-37.35, -26) * mm});
            skLineSegment(sketch, "E91.top", {"start": v(-27.35, -23) * mm, "end": v(-37.35, -23) * mm});
            skLineSegment(sketch, "E91.left", {"start": v(-27.35, -26) * mm, "end": v(-27.35, -23) * mm});
            skLineSegment(sketch, "E91.right", {"start": v(-37.35, -26) * mm, "end": v(-37.35, -23) * mm});
            skSolve(sketch);
        }
        {
            var Q0;
            Q0=makeQuery(id+"F22.imprint","IMPRINT",FACE,{"disambiguationData":[TD([[makeQuery(id+"F22.imprint","IMPRINT",EDGE,{"derivedFrom":sQuery(id+"F22.wireOp",EDGE,"E91.bottom")}),1.0]])]});
            var Q1;
            Q1=makeQuery(id+"F21.boolean.opBoolean","MERGE",FACE,{"derivedFrom":[makeQuery(id+"F19.boolean.opBoolean","MERGE",FACE,{"derivedFrom":[makeQuery(id+"F17.opExtrude","SWEPT_FACE",FACE,{"disambiguationData":[OSD([sQuery(id+"F16.wireOp",EDGE,"E77.MirrorCS")])]}),makeQuery(id+"F19.opExtrude","SWEPT_FACE",FACE,{"disambiguationData":[OSD([sQuery(id+"F18.wireOp",EDGE,"E85.MirrorCS")])]})]}),makeQuery(id+"F21.opExtrude","SWEPT_FACE",FACE,{"disambiguationData":[OSD([sQuery(id+"F20.wireOp",EDGE,"E88.MirrorCS")])]})]});
            extrude(context, id + "F23", {"entities" : qUnion([Q0]), "operationType" : NewBodyOperationType.ADD, "endBound" : BoundingType.UP_TO_SURFACE, "endBoundEntityFace" : qUnion([Q1]), "depth" : 25 * mm});
        }
        {
            var Q0;
            Q0=makeQuery(id+"F23.boolean.opBoolean","MERGE",FACE,{"derivedFrom":[makeQuery(id+"F21.opExtrude","CAP_FACE",FACE,{"disambiguationData":[OSD([sQuery(id+"F20.wireOp",EDGE,"E86.bottom"),sQuery(id+"F20.wireOp",EDGE,"E86.top"),sQuery(id+"F20.wireOp",EDGE,"E86.left"),sQuery(id+"F20.wireOp",EDGE,"E86.right")])],"isStart":false}),makeQuery(id+"F21.opExtrude","CAP_FACE",FACE,{"disambiguationData":[OSD([sQuery(id+"F20.wireOp",EDGE,"E87.MirrorCS"),sQuery(id+"F20.wireOp",EDGE,"E88.MirrorCS"),sQuery(id+"F20.wireOp",EDGE,"E89.MirrorCS"),sQuery(id+"F20.wireOp",EDGE,"E90.MirrorCS")])],"isStart":false}),makeQuery(id+"F23.opExtrude","SWEPT_FACE",FACE,{"disambiguationData":[OSD([sQuery(id+"F22.wireOp",EDGE,"E91.bottom")])]})]});
            var sketch = newSketch(context, id + "F24", { "sketchPlane" : qUnion([Q0])});
            skLineSegment(sketch, "E92.bottom", {"start": v(-139.28, 27.35) * mm, "end": v(-136.28, 27.35) * mm});
            skLineSegment(sketch, "E92.top", {"start": v(-139.28, 37.35) * mm, "end": v(-136.28, 37.35) * mm});
            skLineSegment(sketch, "E92.left", {"start": v(-139.28, 27.35) * mm, "end": v(-139.28, 37.35) * mm});
            skLineSegment(sketch, "E92.right", {"start": v(-136.28, 27.35) * mm, "end": v(-136.28, 37.35) * mm});
            skSolve(sketch);
        }
        {
            var Q0;
            Q0=makeQuery(id+"F24.imprint","IMPRINT",FACE,{"disambiguationData":[TD([[makeQuery(id+"F24.imprint","IMPRINT",EDGE,{"derivedFrom":sQuery(id+"F24.wireOp",EDGE,"E92.bottom")}),1.0]])]});
            extrude(context, id + "F25", {"entities" : qUnion([Q0]), "operationType" : NewBodyOperationType.ADD, "depth" : 45 * mm});
        }
        {
            var Q0;
            Q0=makeQuery(id+"F25.opExtrude","SWEPT_FACE",FACE,{"disambiguationData":[OSD([sQuery(id+"F24.wireOp",EDGE,"E92.right")])]});
            var sketch = newSketch(context, id + "F26", { "sketchPlane" : qUnion([Q0])});
            skLineSegment(sketch, "E93.bottom", {"start": v(-27.35, -71) * mm, "end": v(-37.35, -71) * mm});
            skLineSegment(sketch, "E93.top", {"start": v(-27.35, -68) * mm, "end": v(-37.35, -68) * mm});
            skLineSegment(sketch, "E93.left", {"start": v(-27.35, -71) * mm, "end": v(-27.35, -68) * mm});
            skLineSegment(sketch, "E93.right", {"start": v(-37.35, -71) * mm, "end": v(-37.35, -68) * mm});
            skSolve(sketch);
        }
        {
            var Q0;
            Q0=makeQuery(id+"F26.imprint","IMPRINT",FACE,{"disambiguationData":[TD([[makeQuery(id+"F26.imprint","IMPRINT",EDGE,{"derivedFrom":sQuery(id+"F26.wireOp",EDGE,"E93.bottom")}),-1.0]])]});
            var Q1;
            Q1=makeQuery(id+"F21.boolean.opBoolean","MERGE",FACE,{"derivedFrom":[makeQuery(id+"F19.boolean.opBoolean","MERGE",FACE,{"derivedFrom":[makeQuery(id+"F17.opExtrude","SWEPT_FACE",FACE,{"disambiguationData":[OSD([sQuery(id+"F16.wireOp",EDGE,"E79.MirrorCS")])]}),makeQuery(id+"F19.opExtrude","SWEPT_FACE",FACE,{"disambiguationData":[OSD([sQuery(id+"F18.wireOp",EDGE,"E83.MirrorCS")])]})]}),makeQuery(id+"F21.opExtrude","SWEPT_FACE",FACE,{"disambiguationData":[OSD([sQuery(id+"F20.wireOp",EDGE,"E89.MirrorCS")])]})]});
            extrude(context, id + "F27", {"entities" : qUnion([Q0]), "operationType" : NewBodyOperationType.ADD, "endBound" : BoundingType.UP_TO_SURFACE, "endBoundEntityFace" : qUnion([Q1]), "depth" : 25 * mm});
        }
        {
            var Q0;
            Q0=makeQuery(id+"F27.opExtrude","SWEPT_FACE",FACE,{"disambiguationData":[OSD([sQuery(id+"F26.wireOp",EDGE,"E93.top")])]});
            var sketch = newSketch(context, id + "F28", { "sketchPlane" : qUnion([Q0])});
            skLineSegment(sketch, "E94.bottom", {"start": v(105.72, -27.35) * mm, "end": v(102.72, -27.35) * mm});
            skLineSegment(sketch, "E94.top", {"start": v(105.72, -37.35) * mm, "end": v(102.72, -37.35) * mm});
            skLineSegment(sketch, "E94.left", {"start": v(105.72, -27.35) * mm, "end": v(105.72, -37.35) * mm});
            skLineSegment(sketch, "E94.right", {"start": v(102.72, -27.35) * mm, "end": v(102.72, -37.35) * mm});
            skSolve(sketch);
        }
        {
            var Q0;
            Q0=makeQuery(id+"F28.imprint","IMPRINT",FACE,{"disambiguationData":[TD([[makeQuery(id+"F28.imprint","IMPRINT",EDGE,{"derivedFrom":sQuery(id+"F28.wireOp",EDGE,"E94.bottom")}),1.0]])]});
            extrude(context, id + "F29", {"entities" : qUnion([Q0]), "operationType" : NewBodyOperationType.ADD, "depth" : 20 * mm});
        }
        {
            var Q0;
            Q0=makeQuery(id+"F17.opExtrude","SWEPT_EDGE",EDGE,{"disambiguationData":[OSD([sQuery(id+"F16.wireOp",EDGE,"E74.top"),sQuery(id+"F16.wireOp",EDGE,"E74.left")])]});
            var Q1;
            Q1=makeQuery(id+"F17.opExtrude","SWEPT_EDGE",EDGE,{"disambiguationData":[OSD([sQuery(id+"F16.wireOp",EDGE,"E74.top"),sQuery(id+"F16.wireOp",EDGE,"E74.right")])]});
            var Q2;
            Q2=makeQuery(id+"F17.opExtrude","CAP_EDGE",EDGE,{"disambiguationData":[OSD([sQuery(id+"F16.wireOp",EDGE,"E74.bottom")])],"isStart":true});
            var Q3;
            Q3=makeQuery(id+"F21.opExtrude","CAP_EDGE",EDGE,{"disambiguationData":[OSD([sQuery(id+"F20.wireOp",EDGE,"E86.bottom")])],"isStart":false});
            var Q4;
            Q4=makeQuery(id+"F17.opExtrude","CAP_EDGE",EDGE,{"disambiguationData":[OSD([sQuery(id+"F16.wireOp",EDGE,"E80.MirrorCS")])],"isStart":true});
            var Q5;
            Q5=makeQuery(id+"F21.opExtrude","CAP_EDGE",EDGE,{"disambiguationData":[OSD([sQuery(id+"F20.wireOp",EDGE,"E87.MirrorCS")])],"isStart":false});
            var Q6;
            Q6=makeQuery(id+"F17.opExtrude","SWEPT_EDGE",EDGE,{"disambiguationData":[OSD([sQuery(id+"F16.wireOp",EDGE,"E77.MirrorCS"),sQuery(id+"F16.wireOp",EDGE,"E78.MirrorCS")])]});
            var Q7;
            Q7=makeQuery(id+"F17.opExtrude","SWEPT_EDGE",EDGE,{"disambiguationData":[OSD([sQuery(id+"F16.wireOp",EDGE,"E78.MirrorCS"),sQuery(id+"F16.wireOp",EDGE,"E79.MirrorCS")])]});
            var Q8;
            Q8=makeQuery(id+"F25.opExtrude","CAP_EDGE",EDGE,{"disambiguationData":[OSD([sQuery(id+"F24.wireOp",EDGE,"E92.left")])],"isStart":false});
            var Q9;
            Q9=makeQuery(id+"F27.opExtrude","CAP_EDGE",EDGE,{"disambiguationData":[OSD([sQuery(id+"F26.wireOp",EDGE,"E93.bottom")])],"isStart":false});
            var Q10;
            Q10=makeQuery(id+"F29.opExtrude","CAP_EDGE",EDGE,{"disambiguationData":[OSD([sQuery(id+"F28.wireOp",EDGE,"E94.top")])],"isStart":false});
            var Q11;
            Q11=makeQuery(id+"F29.opExtrude","CAP_EDGE",EDGE,{"disambiguationData":[OSD([sQuery(id+"F28.wireOp",EDGE,"E94.bottom")])],"isStart":false});
            fillet(context, id + "F30", {"entities" : qUnion([Q0, Q1, Q2, Q3, Q4, Q5, Q6, Q7, Q8, Q9, Q10, Q11]), "radius" : 1 * mm, "tangentPropagation" : true, "allowEdgeOverflow" : false});
        }
        {
            var Q0;
            Q0=makeQuery(id+"F17.opExtrude","CAP_FACE",FACE,{"disambiguationData":[OSD([sQuery(id+"F16.wireOp",EDGE,"E77.MirrorCS"),sQuery(id+"F16.wireOp",EDGE,"E78.MirrorCS"),sQuery(id+"F16.wireOp",EDGE,"E79.MirrorCS"),sQuery(id+"F16.wireOp",EDGE,"E80.MirrorCS")])],"isStart":false});
            var sketch = newSketch(context, id + "F31", { "sketchPlane" : qUnion([Q0])});
            skLineSegment(sketch, "E95.bottom", {"start": v(96.64, 52.73) * mm, "end": v(104.64, 52.73) * mm, "construction": true});
            skLineSegment(sketch, "E95.top", {"start": v(96.64, 35.73) * mm, "end": v(104.64, 35.73) * mm, "construction": true});
            skLineSegment(sketch, "E95.left", {"start": v(96.64, 52.73) * mm, "end": v(96.64, 35.73) * mm});
            skLineSegment(sketch, "E95.right", {"start": v(104.64, 52.73) * mm, "end": v(104.64, 35.73) * mm});
            skLineSegment(sketch, "E96", {"start": v(-129.28, 61.35) * mm, "end": v(95.72, 61.35) * mm, "construction": true});
            skLineSegment(sketch, "E97", {"start": v(-16.78, 79.05) * mm, "end": v(-16.78, 61.35) * mm, "construction": true});
            skArc(sketch, "E98", {"start": v(96.64, 35.73) * mm, "mid": v(100.64, 31.73) * mm, "end": v(104.64, 35.73) * mm});
            skArc(sketch, "E99", {"start": v(104.64, 52.73) * mm, "mid": v(100.64, 56.73) * mm, "end": v(96.64, 52.73) * mm});
            skArc(sketch, "E100.MirrorCS", {"start": v(96.64, 86.97) * mm, "mid": v(100.64, 90.97) * mm, "end": v(104.64, 86.97) * mm});
            skLineSegment(sketch, "E101.MirrorCS", {"start": v(96.64, 69.97) * mm, "end": v(96.64, 86.97) * mm});
            skLineSegment(sketch, "E102.MirrorCS", {"start": v(104.64, 69.97) * mm, "end": v(104.64, 86.97) * mm});
            skArc(sketch, "E103.MirrorCS", {"start": v(104.64, 69.97) * mm, "mid": v(100.64, 65.97) * mm, "end": v(96.64, 69.97) * mm});
            skArc(sketch, "E104.MirrorCS", {"start": v(-130.2, 35.73) * mm, "mid": v(-134.2, 31.73) * mm, "end": v(-138.2, 35.73) * mm});
            skLineSegment(sketch, "E105.MirrorCS", {"start": v(-130.2, 52.73) * mm, "end": v(-130.2, 35.73) * mm});
            skLineSegment(sketch, "E106.MirrorCS", {"start": v(-138.2, 52.73) * mm, "end": v(-138.2, 35.73) * mm});
            skArc(sketch, "E107.MirrorCS", {"start": v(-138.2, 52.73) * mm, "mid": v(-134.2, 56.73) * mm, "end": v(-130.2, 52.73) * mm});
            skArc(sketch, "E108.MirrorCS", {"start": v(-138.2, 69.97) * mm, "mid": v(-134.2, 65.97) * mm, "end": v(-130.2, 69.97) * mm});
            skLineSegment(sketch, "E109.MirrorCS", {"start": v(-130.2, 69.97) * mm, "end": v(-130.2, 86.97) * mm});
            skArc(sketch, "E110.MirrorCS", {"start": v(-130.2, 86.97) * mm, "mid": v(-134.2, 90.97) * mm, "end": v(-138.2, 86.97) * mm});
            skLineSegment(sketch, "E111.MirrorCS", {"start": v(-138.2, 69.97) * mm, "end": v(-138.2, 86.97) * mm});
            skPoint(sketch, "E112", {"position": v(95.72, 61.35) * mm});
            skSolve(sketch);
        }
        {
            var Q0;
            Q0=makeQuery(id+"F31.imprint","IMPRINT",FACE,{"disambiguationData":[TD([[makeQuery(id+"F31.imprint","IMPRINT",EDGE,{"derivedFrom":sQuery(id+"F31.wireOp",EDGE,"E104.MirrorCS")}),-1.0]])]});
            var Q1;
            Q1=makeQuery(id+"F31.imprint","IMPRINT",FACE,{"disambiguationData":[TD([[makeQuery(id+"F31.imprint","IMPRINT",EDGE,{"derivedFrom":sQuery(id+"F31.wireOp",EDGE,"E95.left")}),1.0]])]});
            var Q2;
            Q2=makeQuery(id+"F31.imprint","IMPRINT",FACE,{"disambiguationData":[TD([[makeQuery(id+"F31.imprint","IMPRINT",EDGE,{"derivedFrom":sQuery(id+"F31.wireOp",EDGE,"E100.MirrorCS")}),-1.0]])]});
            var Q3;
            Q3=makeQuery(id+"F31.imprint","IMPRINT",FACE,{"disambiguationData":[TD([[makeQuery(id+"F31.imprint","IMPRINT",EDGE,{"derivedFrom":sQuery(id+"F31.wireOp",EDGE,"E108.MirrorCS")}),1.0]])]});
            extrude(context, id + "F32", {"entities" : qUnion([Q0, Q1, Q2, Q3]), "depth" : 1 * mm});
        }
    });
